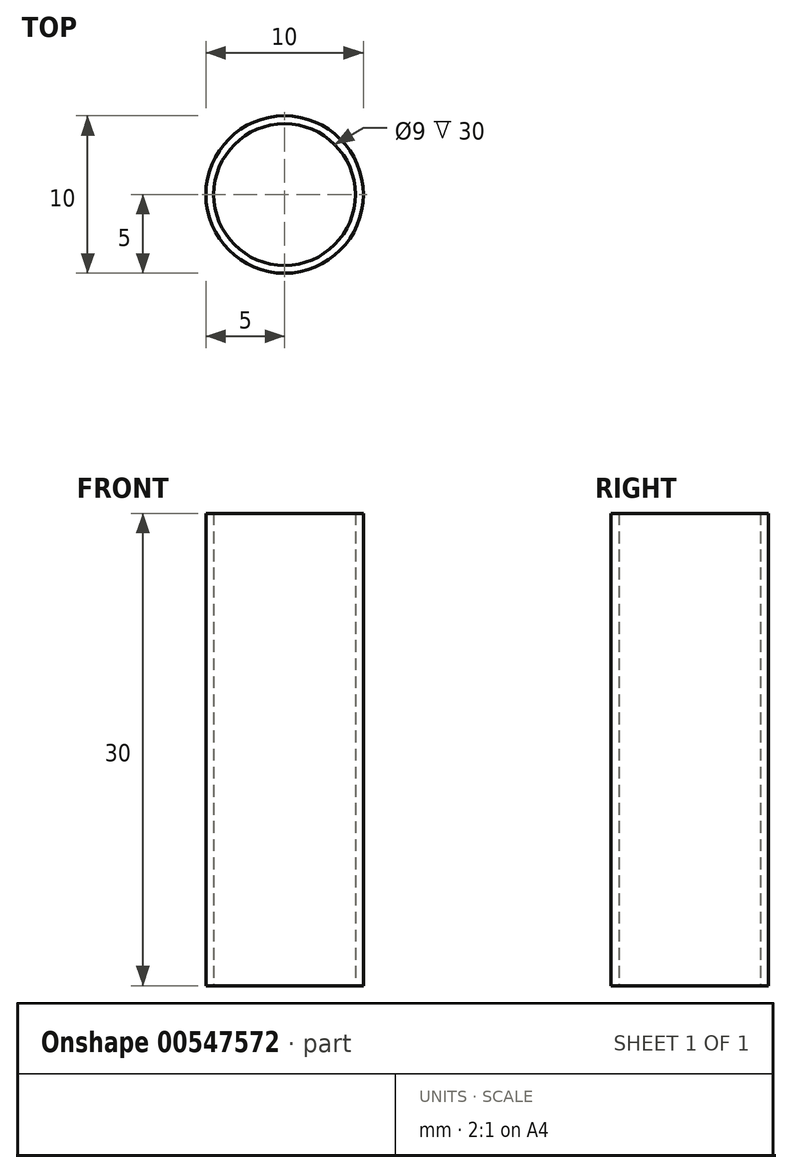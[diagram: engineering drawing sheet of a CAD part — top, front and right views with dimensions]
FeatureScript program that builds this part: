
annotation { "Feature Type Name" : "Feature", "Feature Type Description" : "" }
export const myFeature = defineFeature(function(context is Context, id is Id, definition is map)
    precondition{}
    {
        {
            var Q0;
            Q0=qCreatedBy(makeId("Top.planeOp"),FACE);
            var sketch = newSketch(context, id + "F0", { "sketchPlane" : qUnion([Q0])});
            skCircle(sketch, "E0", {"center": v(0, 0) * mm, "radius": 5 * mm});
            skCircle(sketch, "E1", {"center": v(0, 0) * mm, "radius": 4.5 * mm});
            skSolve(sketch);
        }
        {
            var Q0;
            Q0 = qSketchRegion(id + "F0", true);
            extrude(context, id + "F1", {"entities" : qUnion([Q0]), "depth" : 30 * mm, "offsetDistance" : 25.4 * mm});
        }
    });
